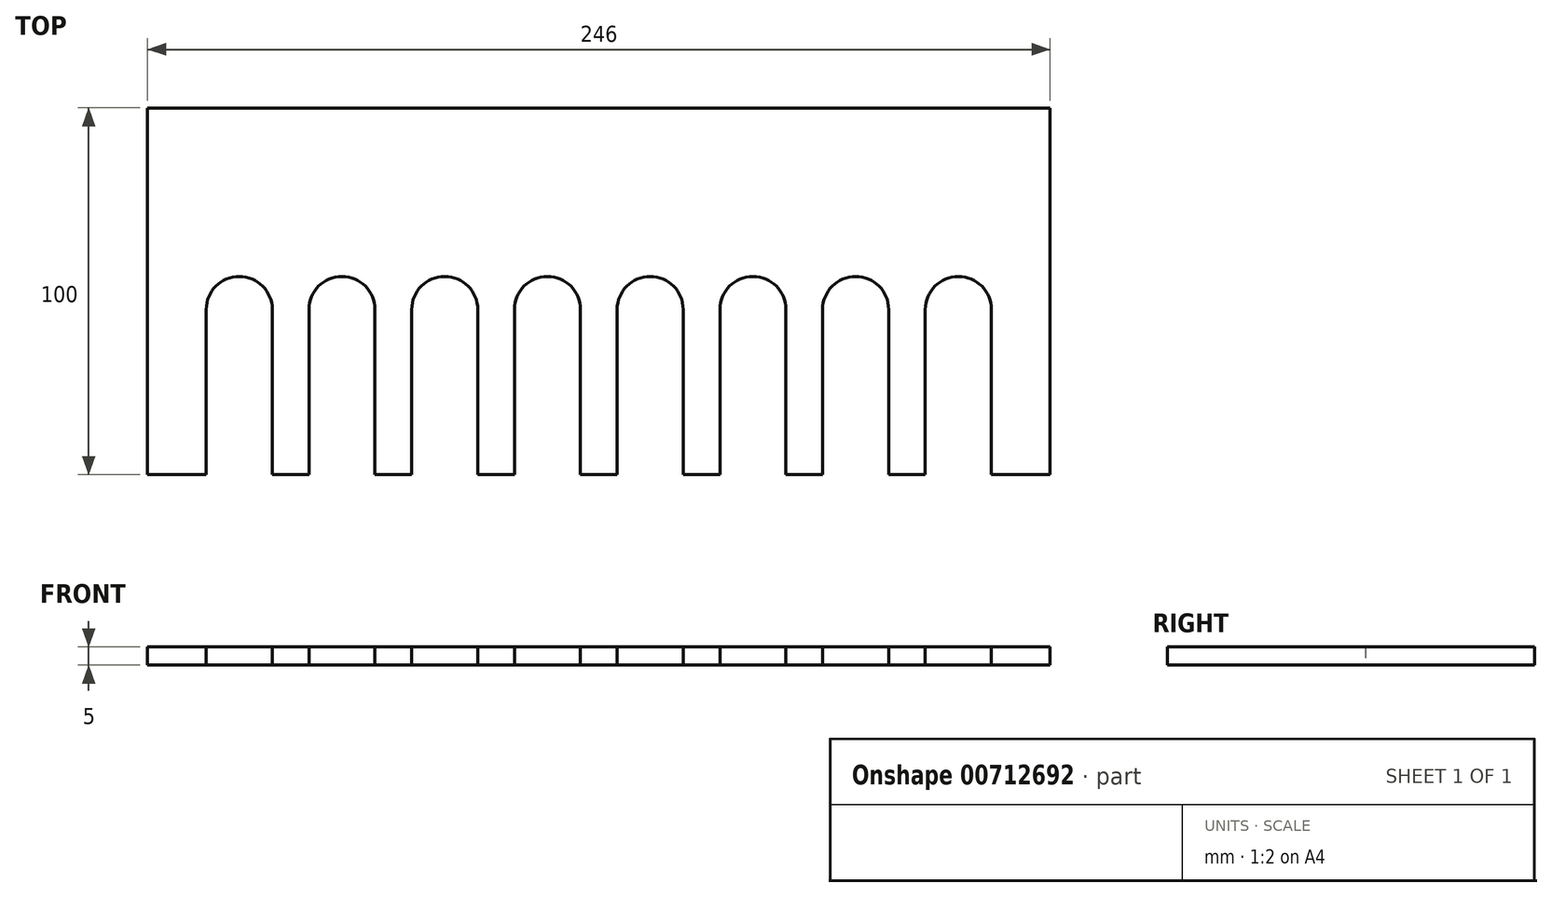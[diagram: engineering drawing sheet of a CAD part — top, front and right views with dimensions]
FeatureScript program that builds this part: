
annotation { "Feature Type Name" : "Feature", "Feature Type Description" : "" }
export const myFeature = defineFeature(function(context is Context, id is Id, definition is map)
    precondition{}
    {
        {
            var Q0;
            Q0=qCreatedBy(makeId("Top.planeOp"),FACE);
            var sketch = newSketch(context, id + "F0", { "sketchPlane" : qUnion([Q0])});
            skPoint(sketch, "E0.0.internal.orphan", {"position": v(33.76, 61.1) * mm});
            skPoint(sketch, "E0.1.internal.orphan", {"position": v(24.86, 61.1) * mm});
            skPoint(sketch, "E1.bottom.start.orphan", {"position": v(6.94, 75.72) * mm});
            skPoint(sketch, "E1.top.start.orphan", {"position": v(6.94, 125.72) * mm});
            skLineSegment(sketch, "E2", {"start": v(13.98, 96.92) * mm, "end": v(13.98, 96.92) * mm});
            skLineSegment(sketch, "E3.left", {"start": v(-417.64, -70.6) * mm, "end": v(-417.64, -170.6) * mm});
            skLineSegment(sketch, "E4", {"start": v(-417.64, -170.6) * mm, "end": v(-401.64, -170.6) * mm});
            skLineSegment(sketch, "E5", {"start": v(-401.64, -170.6) * mm, "end": v(-401.64, -125.6) * mm});
            skPoint(sketch, "E6.end.orphan", {"position": v(-385.64, -170.6) * mm});
            skLineSegment(sketch, "E7", {"start": v(-383.64, -125.6) * mm, "end": v(-383.64, -170.6) * mm});
            skLineSegment(sketch, "E8", {"start": v(-383.64, -170.6) * mm, "end": v(-373.64, -170.6) * mm});
            skLineSegment(sketch, "E9", {"start": v(-373.64, -170.6) * mm, "end": v(-373.64, -125.6) * mm});
            skLineSegment(sketch, "E10", {"start": v(-355.64, -130.58) * mm, "end": v(-355.64, -170.6) * mm});
            skLineSegment(sketch, "E11", {"start": v(-355.64, -170.6) * mm, "end": v(-345.64, -170.6) * mm});
            skLineSegment(sketch, "E12", {"start": v(-345.64, -170.6) * mm, "end": v(-345.64, -125.6) * mm});
            skPoint(sketch, "E13.start.orphan", {"position": v(-335.64, -170.6) * mm});
            skPoint(sketch, "E14.start.orphan", {"position": v(-325.64, -125.6) * mm});
            skPoint(sketch, "E15.end.orphan", {"position": v(-315.64, -170.6) * mm});
            skLineSegment(sketch, "E16", {"start": v(-327.64, -125.58) * mm, "end": v(-327.64, -170.58) * mm});
            skLineSegment(sketch, "E17", {"start": v(-327.64, -170.58) * mm, "end": v(-317.64, -170.58) * mm});
            skLineSegment(sketch, "E18", {"start": v(-317.64, -170.58) * mm, "end": v(-317.64, -125.6) * mm});
            skLineSegment(sketch, "E19", {"start": v(-299.64, -125.6) * mm, "end": v(-299.64, -170.58) * mm});
            skLineSegment(sketch, "E20", {"start": v(-299.64, -170.58) * mm, "end": v(-289.64, -170.58) * mm});
            skLineSegment(sketch, "E21", {"start": v(-289.64, -170.58) * mm, "end": v(-289.64, -125.6) * mm});
            skLineSegment(sketch, "E22", {"start": v(-271.64, -125.6) * mm, "end": v(-271.64, -170.58) * mm});
            skLineSegment(sketch, "E23", {"start": v(-271.64, -170.58) * mm, "end": v(-261.64, -170.58) * mm});
            skLineSegment(sketch, "E24", {"start": v(-261.64, -170.58) * mm, "end": v(-261.64, -125.6) * mm});
            skLineSegment(sketch, "E25", {"start": v(-243.64, -125.6) * mm, "end": v(-243.64, -170.58) * mm});
            skLineSegment(sketch, "E26", {"start": v(-243.64, -170.58) * mm, "end": v(-233.64, -170.58) * mm});
            skLineSegment(sketch, "E27", {"start": v(-233.64, -170.58) * mm, "end": v(-233.64, -125.6) * mm});
            skLineSegment(sketch, "E28", {"start": v(-215.64, -125.6) * mm, "end": v(-215.64, -170.58) * mm});
            skLineSegment(sketch, "E29", {"start": v(-215.64, -170.58) * mm, "end": v(-205.64, -170.58) * mm});
            skLineSegment(sketch, "E30", {"start": v(-205.64, -170.58) * mm, "end": v(-205.64, -125.6) * mm});
            skLineSegment(sketch, "E31", {"start": v(-187.64, -125.6) * mm, "end": v(-187.64, -170.58) * mm});
            skLineSegment(sketch, "E32", {"start": v(-187.64, -170.58) * mm, "end": v(-171.64, -170.58) * mm});
            skLineSegment(sketch, "E33", {"start": v(-171.64, -170.58) * mm, "end": v(-171.64, -70.58) * mm});
            skLineSegment(sketch, "E34", {"start": v(-417.64, -70.6) * mm, "end": v(-171.64, -70.6) * mm});
            skPoint(sketch, "E35.visualSharp", {"position": v(-355.64, -125.6) * mm});
            skLineSegment(sketch, "E36", {"start": v(-355.64, -130.58) * mm, "end": v(-355.64, -125.6) * mm});
            skArc(sketch, "E37", {"start": v(-327.64, -125.58) * mm, "mid": v(-336.64, -116.58) * mm, "end": v(-345.64, -125.6) * mm});
            skArc(sketch, "E38", {"start": v(-355.64, -125.6) * mm, "mid": v(-364.64, -116.6) * mm, "end": v(-373.64, -125.6) * mm});
            skArc(sketch, "E39", {"start": v(-383.64, -125.6) * mm, "mid": v(-392.64, -116.6) * mm, "end": v(-401.64, -125.6) * mm});
            skArc(sketch, "E40", {"start": v(-299.64, -125.6) * mm, "mid": v(-308.64, -116.6) * mm, "end": v(-317.64, -125.6) * mm});
            skArc(sketch, "E41", {"start": v(-271.64, -125.6) * mm, "mid": v(-280.64, -116.6) * mm, "end": v(-289.64, -125.6) * mm});
            skArc(sketch, "E42", {"start": v(-243.64, -125.6) * mm, "mid": v(-252.64, -116.6) * mm, "end": v(-261.64, -125.6) * mm});
            skArc(sketch, "E43", {"start": v(-215.64, -125.6) * mm, "mid": v(-224.64, -116.6) * mm, "end": v(-233.64, -125.6) * mm});
            skArc(sketch, "E44", {"start": v(-187.64, -125.6) * mm, "mid": v(-196.64, -116.6) * mm, "end": v(-205.64, -125.6) * mm});
            skSolve(sketch);
        }
        {
            var Q0;
            Q0=makeQuery(id+"F0.imprint","IMPRINT",FACE,{"disambiguationData":[TD([[makeQuery(id+"F0.imprint","IMPRINT",EDGE,{"derivedFrom":sQuery(id+"F0.wireOp",EDGE,"E3.left")}),1.0]])]});
            extrude(context, id + "F1", {"entities" : qUnion([Q0]), "depth" : 5 * mm, "offsetDistance" : 25 * mm});
        }
    });
